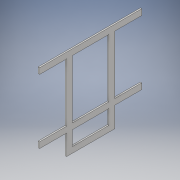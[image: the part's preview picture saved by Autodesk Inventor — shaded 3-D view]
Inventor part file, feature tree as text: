
AUTODESK INVENTOR PART (.ipt)
format: ipt  version: 2017 (Build 210142000, 142)  size: 130,560 bytes
history: native  units: in
note: dims shown in document units (in); Inventor stores cm internally (conversion verified against a paired STEP export)
features: extrude x1, sketch x1
ambient origin geometry x8: Origin, YZ Plane, XZ Plane, XY Plane, X Axis, Y Axis, Z Axis, Center Point
bodies: Body1 (feature_tree)
feature tree (2):
  extrude  "Extrusion2"  Depth=17.5in
  sketch  "Sketch1"  dims[d0=4.5in d1=17.5in d2=3.5in d3=8.234in d4=4.633in d9=2.5in d10=6.234in d11=1.0in d12=1.0in d16=10.0in d17=0.25in d18=0.0in d24=4.633in d25=1.0in d26=4.633in d27=1.0in d28=15.5in]
